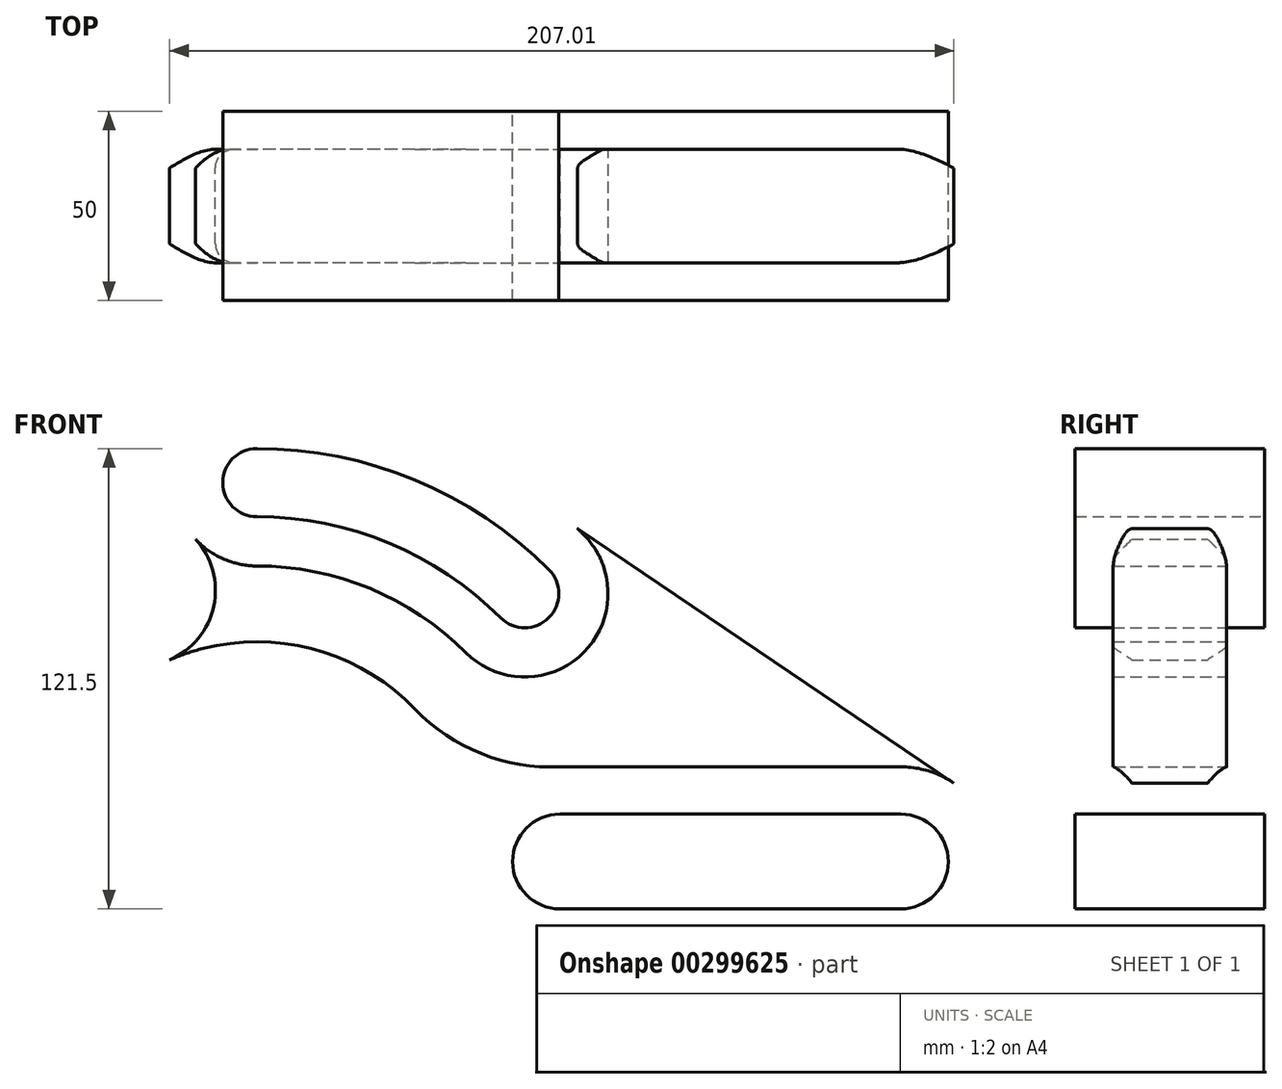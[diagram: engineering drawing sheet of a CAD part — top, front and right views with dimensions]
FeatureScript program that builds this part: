
annotation { "Feature Type Name" : "Feature", "Feature Type Description" : "" }
export const myFeature = defineFeature(function(context is Context, id is Id, definition is map)
    precondition{}
    {
        {
            var Q0;
            Q0=qCreatedBy(makeId("Front.planeOp"),FACE);
            var sketch = newSketch(context, id + "F0", { "sketchPlane" : qUnion([Q0])});
            skLineSegment(sketch, "E0", {"start": v(80, 0) * mm, "end": v(170, 0) * mm, "construction": true});
            skArc(sketch, "E1.0.startCap", {"start": v(80, -12.5) * mm, "mid": v(67.5, 0) * mm, "end": v(80, 12.5) * mm});
            skArc(sketch, "E1.0.endCap", {"start": v(170, 12.5) * mm, "mid": v(182.5, 0) * mm, "end": v(170, -12.5) * mm});
            skLineSegment(sketch, "E1.0.left", {"start": v(80, 12.5) * mm, "end": v(170, 12.5) * mm});
            skLineSegment(sketch, "E1.0.right", {"start": v(80, -12.5) * mm, "end": v(170, -12.5) * mm});
            skCircle(sketch, "E2", {"center": v(0, 0) * mm, "radius": 40 * mm});
            skLineSegment(sketch, "E3.0", {"start": v(77.71, -25) * mm, "end": v(170, -25) * mm});
            skArc(sketch, "E3.1", {"start": v(170, 25) * mm, "mid": v(195, 0) * mm, "end": v(170, -25) * mm});
            skLineSegment(sketch, "E3.2", {"start": v(80, 25) * mm, "end": v(170, 25) * mm});
            skArc(sketch, "E4", {"start": v(41.73, -40.28) * mm, "mid": v(-58, 0.02) * mm, "end": v(41.76, 40.25) * mm});
            skArc(sketch, "E5", {"start": v(41.76, 40.25) * mm, "mid": v(59.24, 28.5) * mm, "end": v(80, 25) * mm});
            skArc(sketch, "E6", {"start": v(77.71, -25) * mm, "mid": v(58.17, -28.98) * mm, "end": v(41.73, -40.28) * mm});
            skArc(sketch, "E7", {"start": v(0, 100) * mm, "mid": v(38.27, 92.39) * mm, "end": v(70.71, 70.71) * mm, "construction": true});
            skArc(sketch, "E8.0.startCap", {"start": v(0, 91) * mm, "mid": v(-9, 100) * mm, "end": v(0, 109) * mm});
            skArc(sketch, "E8.0.endCap", {"start": v(77.07, 77.07) * mm, "mid": v(77.07, 64.35) * mm, "end": v(64.35, 64.35) * mm});
            skArc(sketch, "E8.0.left", {"start": v(0, 109) * mm, "mid": v(41.71, 100.7) * mm, "end": v(77.07, 77.07) * mm});
            skArc(sketch, "E8.0.right", {"start": v(0, 91) * mm, "mid": v(34.82, 84.07) * mm, "end": v(64.35, 64.35) * mm});
            skArc(sketch, "E9.0", {"start": v(0, 122) * mm, "mid": v(46.69, 112.71) * mm, "end": v(86.27, 86.27) * mm});
            skArc(sketch, "E9.1", {"start": v(0, 78) * mm, "mid": v(-22, 100) * mm, "end": v(0, 122) * mm});
            skArc(sketch, "E9.2", {"start": v(0, 78) * mm, "mid": v(29.85, 72.06) * mm, "end": v(55.15, 55.15) * mm});
            skArc(sketch, "E9.3", {"start": v(86.27, 86.27) * mm, "mid": v(86.27, 55.15) * mm, "end": v(55.15, 55.15) * mm});
            skArc(sketch, "E10", {"start": v(-23, 53.24) * mm, "mid": v(-11.38, 67.43) * mm, "end": v(-16.2, 85.12) * mm});
            skLineSegment(sketch, "E11", {"start": v(70.71, 70.71) * mm, "end": v(86.27, 86.27) * mm, "construction": true});
            skLineSegment(sketch, "E12", {"start": v(0, 100) * mm, "end": v(0, 122) * mm, "construction": true});
            skLineSegment(sketch, "E13", {"start": v(83.03, 88.94) * mm, "end": v(184, 20.71) * mm});
            skSolve(sketch);
        }
        {
            var Q0;
            Q0=makeQuery(id+"F0.imprint","IMPRINT",FACE,{"disambiguationData":[TD([[makeQuery(id+"F0.imprint","IMPRINT",EDGE,{"derivedFrom":sQuery(id+"F0.wireOp",EDGE,"E1.0.startCap")}),1.0]])]});
            extrude(context, id + "F1", {"entities" : qUnion([Q0]), "endBound" : BoundingType.SYMMETRIC, "depth" : 50 * mm});
        }
        {
            var Q0;
            Q0=makeQuery(id+"F0.imprint","IMPRINT",FACE,{"disambiguationData":[TD([[makeQuery(id+"F0.imprint","IMPRINT",EDGE,{"derivedFrom":sQuery(id+"F0.wireOp",EDGE,"E8.0.startCap")}),1.0]])]});
            extrude(context, id + "F2", {"entities" : qUnion([Q0]), "endBound" : BoundingType.SYMMETRIC, "depth" : 50 * mm});
        }
        {
            var Q0;
            {var subQ4=sQuery(id+"F0.wireOp",EDGE,"E3.2");Q0=makeQuery(id+"F0.imprint","IMPRINT",FACE,{"disambiguationData":[TD([[makeQuery(id+"F0.imprint","IMPRINT",EDGE,{"derivedFrom":subQ4}),1.0]])]});}
            extrude(context, id + "F3", {"entities" : qUnion([Q0]), "endBound" : BoundingType.SYMMETRIC, "depth" : 30 * mm});
        }
        {
            var Q0;
            Q0=makeQuery(id+"F1.opExtrude","CAP_EDGE",EDGE,{"disambiguationData":[OSD([sQuery(id+"F0.wireOp",EDGE,"E4")])],"isStart":false});
            var Q1;
            Q1=makeQuery(id+"F2.opExtrude","CAP_EDGE",EDGE,{"disambiguationData":[OSD([sQuery(id+"F0.wireOp",EDGE,"E9.0")])],"isStart":false});
            var Q2;
            Q2=makeQuery(id+"F2.opExtrude","CAP_EDGE",EDGE,{"disambiguationData":[OSD([sQuery(id+"F0.wireOp",EDGE,"E9.0")])],"isStart":true});
            var Q3;
            Q3=makeQuery(id+"F1.opExtrude","CAP_EDGE",EDGE,{"disambiguationData":[OSD([sQuery(id+"F0.wireOp",EDGE,"E4")])],"isStart":true});
            var Q4;
            Q4=makeQuery(id+"F3.opExtrude","CAP_EDGE",EDGE,{"disambiguationData":[OSD([sQuery(id+"F0.wireOp",EDGE,"E13")])],"isStart":false});
            var Q5;
            Q5=makeQuery(id+"F3.opExtrude","CAP_EDGE",EDGE,{"disambiguationData":[OSD([sQuery(id+"F0.wireOp",EDGE,"E13")])],"isStart":true});
            var Q6;
            Q6=makeQuery(id+"F3.opExtrude","CAP_EDGE",EDGE,{"disambiguationData":[OSD([sQuery(id+"F0.wireOp",EDGE,"E10")])],"isStart":false});
            var Q7;
            Q7=makeQuery(id+"F3.opExtrude","CAP_EDGE",EDGE,{"disambiguationData":[OSD([sQuery(id+"F0.wireOp",EDGE,"E10")])],"isStart":true});
            fillet(context, id + "F4", {"entities" : qUnion([Q0, Q1, Q2, Q3, Q4, Q5, Q6, Q7]), "radius" : 5 * mm, "tangentPropagation" : true, "allowEdgeOverflow" : false});
        }
    });
